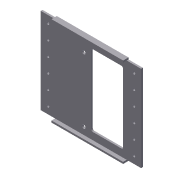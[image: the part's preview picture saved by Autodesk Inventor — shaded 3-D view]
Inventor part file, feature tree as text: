
AUTODESK INVENTOR PART (.ipt)
format: ipt  version: 2012 (Build 160160000, 160)  size: 155,136 bytes
history: native  units: in
note: dims shown in document units (in); Inventor stores cm internally (conversion verified against a paired STEP export)
features: extrude x5, sketch x5
ambient origin geometry x8: Origin, YZ Plane, XZ Plane, XY Plane, X Axis, Y Axis, Z Axis, Center Point
feature tree (10):
  extrude  "Extrusion3"  Depth=7.0in
  extrude  "Extrusion4"  Depth=1.0in
  extrude  "Extrusion5"  Depth=0.125in TaperAngle=0.0deg
  extrude  "Extrusion6"  Depth=1.0in
  extrude  "Extrusion7"  Depth=0.5in
  sketch  "Sketch1"  dims[d0=6.0in d1=7.0in]
  sketch  "Sketch2"  dims[d18=1.0in d19=1.0in]
  sketch  "Sketch3"  dims[d20=0.125in d24=0.125in d25=0.0in]
  sketch  "Sketch4"  dims[d26=0.5in d27=1.0in]
  sketch  "Sketch5"  dims[d28=0.1875in d29=0.5in d30=1.0in d31=0.1875in d32=0.125in d33=0.0in d34=3.0in d35=3.0in d36=4.5in d37=0.5in d38=0.25in d39=0.25in d40=0.125in d41=0.0in d42=0.5in d43=1.25in d44=0.5in d45=0.5in d46=0.125in d47=0.125in d48=0.0in d49=0.25in d50=0.0in]
